# Revit family: Abutment
name_source: partatom
category: Generic Models
units: mm (PartAtom-declared; Revit-internal decimal feet)

## family parameters
Always vertical = Yes
Can host rebar = Yes
Cut with Voids When Loaded = No
Part Type = Normal
Room Calculation Point = No
Round Connector Dimension = Use Diameter
Shared = No
Work Plane-Based = No

## types (1)
- Type 1
    BackWallAdditionalWidth = 0 m
    BackWallCantileverLength = 0 m
    BackWallCantileverThickness = 0 m
    BackWallInnerHeight = 0 m
    BackWallInnerLeftSlope = 0.1
    BackWallInnerRightSlope = 0.1
    BackWallOuterHeight = 1 m
    BackWallOuterLeftSlope = 0.1
    BackWallOuterRightSlope = 0.1
    BackWallSlope = 0.025
    BackWallWidth = 0 m
    BearingShelfSlope = 0.02
    BearingShelfWidth = 1 m
    CornerWallHeight = 1 m
    Default Elevation = 0 m
    DrainageAxisLeft = 2 m
    DrainageAxisRight = 2 m
    FoundationAdding = 0 m
    FoundationHeight = 1 m
    FoundationInnerDropHeight = 0 m
    FoundationInnerWidth = 2 m
    FoundationOuterDropHeight = 0 m
    FoundationOuterWidth = 1 m
    IsBackWallCantilever = No
    IsLeftWing = Yes
    IsLeftWingDilatation = Yes
    IsRightWing = Yes
    IsRightWingDilatation = Yes
    IsStepThicknessChange = No
    LeftWallOuterHeight = 4 m
    LeftWingAdditionalHeight = 4 m
    LeftWingCutHeight = 1 m
    LeftWingCutWidth = 1 m
    LeftWingFoundationAdding = 0 m
    LeftWingFoundationDropHeight = 0 m
    LeftWingFoundationLength = 2 m
    LeftWingFoundationWidth = 1 m
    LeftWingSlope = 0.02
    LeftWingUncutedHeight = 1 m
    Material = C30/37
    RightWallOuterHeight = 4 m
    RightWingAdditionalHeight = 4 m
    RightWingCutHeight = 1 m
    RightWingCutWidth = 1 m
    RightWingFoundationAdding = 0 m
    RightWingFoundationDropHeight = 0 m
    RightWingFoundationLength = 2 m
    RightWingFoundationWidth = 1 m
    RightWingSlope = 0.02
    RightWingUncutedHeight = 1 m
    SkewAngle = 25.00°
    TransitionShelfSlope = 0.1
    Type = Abutment
    WallInnerHeight = 3 m
    WallLength = 7 m
    WallOuterHeight = 4 m
    WallWidth = 1 m
    WingAdditionalSlope = 0.02
    WingAdditionalWidth = 0 m
    WingWidth = 0 m

## geometry (parser evidence)
native form markers: Sweep x3
no freeform markers — native parametric forms only
